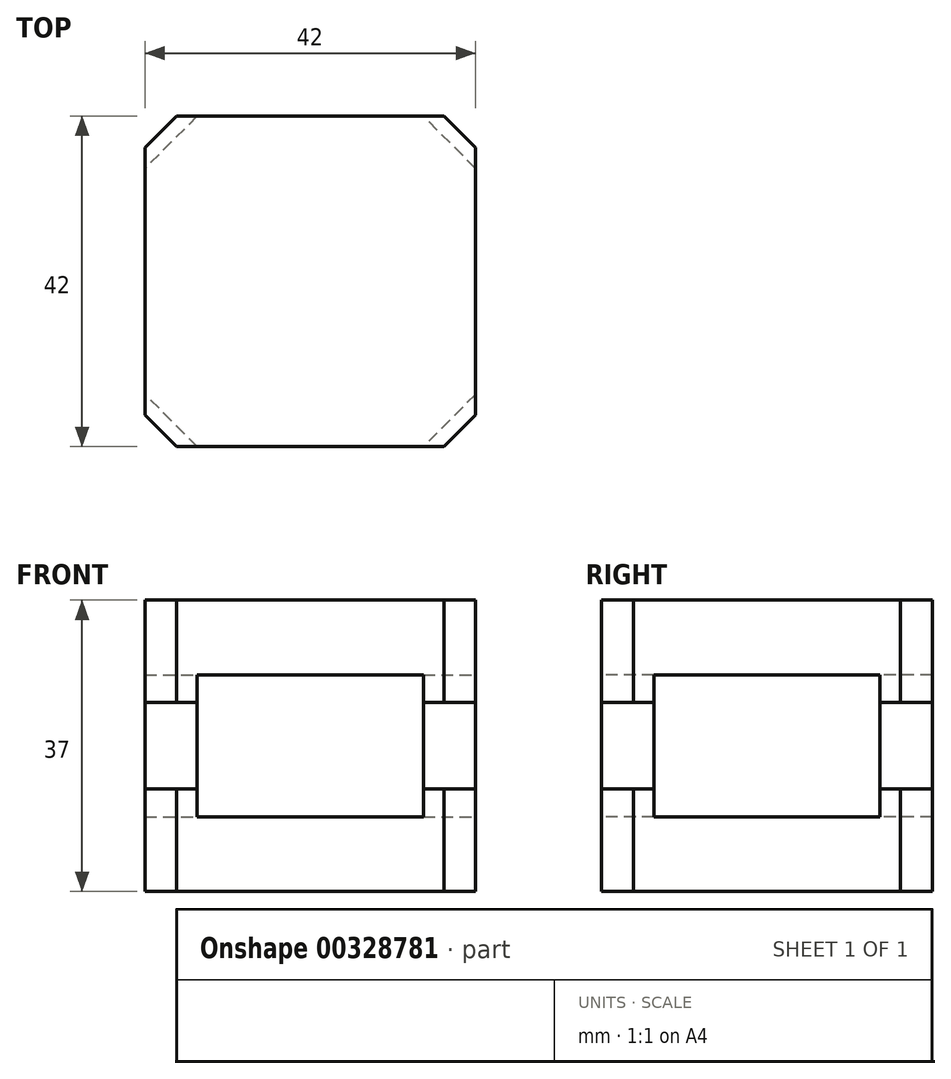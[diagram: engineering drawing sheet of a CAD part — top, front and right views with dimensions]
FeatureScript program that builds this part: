
annotation { "Feature Type Name" : "Feature", "Feature Type Description" : "" }
export const myFeature = defineFeature(function(context is Context, id is Id, definition is map)
    precondition{}
    {
        {
            var Q0;
            Q0=qCreatedBy(makeId("Top.planeOp"),FACE);
            var sketch = newSketch(context, id + "F0", { "sketchPlane" : qUnion([Q0])});
            skLineSegment(sketch, "E0.bottom", {"start": v(16.97, -21) * mm, "end": v(-16.97, -21) * mm});
            skLineSegment(sketch, "E0.top", {"start": v(16.97, 21) * mm, "end": v(-16.97, 21) * mm});
            skLineSegment(sketch, "E0.left", {"start": v(21, -16.97) * mm, "end": v(21, 16.97) * mm});
            skLineSegment(sketch, "E0.right", {"start": v(-21, -16.97) * mm, "end": v(-21, 16.97) * mm});
            skPoint(sketch, "E0.middle", {"position": v(0, 0) * mm});
            skLineSegment(sketch, "E1.bottom", {"start": v(-21, 16.97) * mm, "end": v(-16.97, 21) * mm});
            skLineSegment(sketch, "E1.top", {"start": v(16.97, -21) * mm, "end": v(21, -16.97) * mm});
            skLineSegment(sketch, "E1.left", {"start": v(-21, -16.97) * mm, "end": v(-16.97, -21) * mm});
            skLineSegment(sketch, "E1.right", {"start": v(16.97, 21) * mm, "end": v(21, 16.97) * mm});
            skLineSegment(sketch, "E2", {"start": v(21, 0) * mm, "end": v(0, 0) * mm, "construction": true});
            skLineSegment(sketch, "E3", {"start": v(0, 21) * mm, "end": v(0, 0) * mm, "construction": true});
            skSolve(sketch);
        }
        {
            var Q0;
            Q0=qSketchRegion(id+"F0",true);
            extrude(context, id + "F1", {"entities" : qUnion([Q0]), "depth" : 13 * mm});
        }
        {
            var Q0;
            Q0=qCreatedBy(makeId("Top.planeOp"),FACE);
            cPlane(context, id + "F2", {"entities" : qUnion([Q0]), "cplaneType" : CPlaneType.OFFSET, "offset" : 9.5 * mm, "width" : 150 * mm, "height" : 150 * mm});
        }
        {
            var Q0;
            Q0=qCreatedBy(id+"F2.planeOp",FACE);
            var sketch = newSketch(context, id + "F3", { "sketchPlane" : qUnion([Q0])});
            skLineSegment(sketch, "E4.bottom", {"start": v(14.36, -21) * mm, "end": v(-14.36, -21) * mm});
            skLineSegment(sketch, "E4.top", {"start": v(14.36, 21) * mm, "end": v(-14.36, 21) * mm});
            skLineSegment(sketch, "E4.left", {"start": v(21, -14.36) * mm, "end": v(21, 14.36) * mm});
            skLineSegment(sketch, "E4.right", {"start": v(-21, -14.36) * mm, "end": v(-21, 14.36) * mm});
            skPoint(sketch, "E4.middle", {"position": v(0, 0) * mm});
            skLineSegment(sketch, "E5.bottom", {"start": v(-21, 14.36) * mm, "end": v(-14.36, 21) * mm});
            skLineSegment(sketch, "E5.top", {"start": v(14.36, -21) * mm, "end": v(21, -14.36) * mm});
            skLineSegment(sketch, "E5.left", {"start": v(-21, -14.36) * mm, "end": v(-14.36, -21) * mm});
            skLineSegment(sketch, "E5.right", {"start": v(14.36, 21) * mm, "end": v(21, 14.36) * mm});
            skLineSegment(sketch, "E6", {"start": v(21, 0) * mm, "end": v(0, 0) * mm, "construction": true});
            skLineSegment(sketch, "E7", {"start": v(0, 21) * mm, "end": v(0, 0) * mm, "construction": true});
            skSolve(sketch);
        }
        {
            var Q0;
            Q0=qSketchRegion(id+"F3",true);
            extrude(context, id + "F4", {"entities" : qUnion([Q0]), "depth" : 18 * mm});
        }
        {
            var Q0;
            Q0=makeQuery(id+"F4.opExtrude","SWEPT_BODY",BODY,{"disambiguationData":[OSD([sQuery(id+"F3.wireOp",EDGE,"E4.bottom"),sQuery(id+"F3.wireOp",EDGE,"E4.top"),sQuery(id+"F3.wireOp",EDGE,"E4.left"),sQuery(id+"F3.wireOp",EDGE,"E4.right"),sQuery(id+"F3.wireOp",EDGE,"E5.bottom"),sQuery(id+"F3.wireOp",EDGE,"E5.top"),sQuery(id+"F3.wireOp",EDGE,"E5.left"),sQuery(id+"F3.wireOp",EDGE,"E5.right")])]});
            var Q1;
            Q1=makeQuery(id+"F1.opExtrude","SWEPT_BODY",BODY,{"disambiguationData":[OSD([sQuery(id+"F0.wireOp",EDGE,"E0.bottom"),sQuery(id+"F0.wireOp",EDGE,"E0.top"),sQuery(id+"F0.wireOp",EDGE,"E0.left"),sQuery(id+"F0.wireOp",EDGE,"E0.right"),sQuery(id+"F0.wireOp",EDGE,"E1.bottom"),sQuery(id+"F0.wireOp",EDGE,"E1.top"),sQuery(id+"F0.wireOp",EDGE,"E1.left"),sQuery(id+"F0.wireOp",EDGE,"E1.right")])]});
            booleanBodies(context, id + "F5", {"operationType" : BooleanOperationType.SUBTRACTION, "tools" : qUnion([Q0]), "targets" : qUnion([Q1]), "keepTools" : true});
        }
        {
            var Q0;
            Q0=makeQuery(id+"F4.opExtrude","CAP_FACE",FACE,{"disambiguationData":[OSD([sQuery(id+"F3.wireOp",EDGE,"E4.bottom"),sQuery(id+"F3.wireOp",EDGE,"E4.top"),sQuery(id+"F3.wireOp",EDGE,"E4.left"),sQuery(id+"F3.wireOp",EDGE,"E4.right"),sQuery(id+"F3.wireOp",EDGE,"E5.bottom"),sQuery(id+"F3.wireOp",EDGE,"E5.top"),sQuery(id+"F3.wireOp",EDGE,"E5.left"),sQuery(id+"F3.wireOp",EDGE,"E5.right")])],"isStart":false});
            cPlane(context, id + "F6", {"entities" : qUnion([Q0]), "cplaneType" : CPlaneType.OFFSET, "offset" : 3.5 * mm, "oppositeDirection" : true, "width" : 150 * mm, "height" : 150 * mm});
        }
        {
            var Q0;
            Q0=qCreatedBy(id+"F6.planeOp",FACE);
            var sketch = newSketch(context, id + "F7", { "sketchPlane" : qUnion([Q0])});
            skLineSegment(sketch, "E8.bottom", {"start": v(16.97, -21) * mm, "end": v(-16.97, -21) * mm});
            skLineSegment(sketch, "E8.top", {"start": v(16.97, 21) * mm, "end": v(-16.97, 21) * mm});
            skLineSegment(sketch, "E8.left", {"start": v(21, -16.97) * mm, "end": v(21, 16.97) * mm});
            skLineSegment(sketch, "E8.right", {"start": v(-21, -16.97) * mm, "end": v(-21, 16.97) * mm});
            skPoint(sketch, "E8.middle", {"position": v(0, 0) * mm});
            skLineSegment(sketch, "E9.bottom", {"start": v(-21, 16.97) * mm, "end": v(-16.97, 21) * mm});
            skLineSegment(sketch, "E9.top", {"start": v(16.97, -21) * mm, "end": v(21, -16.97) * mm});
            skLineSegment(sketch, "E9.left", {"start": v(-21, -16.97) * mm, "end": v(-16.97, -21) * mm});
            skLineSegment(sketch, "E9.right", {"start": v(16.97, 21) * mm, "end": v(21, 16.97) * mm});
            skLineSegment(sketch, "E10", {"start": v(21, 0) * mm, "end": v(0, 0) * mm, "construction": true});
            skLineSegment(sketch, "E11", {"start": v(0, 21) * mm, "end": v(0, 0) * mm, "construction": true});
            skSolve(sketch);
        }
        {
            var Q0;
            Q0=qSketchRegion(id+"F7",true);
            extrude(context, id + "F8", {"entities" : qUnion([Q0]), "depth" : 13 * mm});
        }
        {
            var Q0;
            Q0=makeQuery(id+"F4.opExtrude","SWEPT_BODY",BODY,{"disambiguationData":[OSD([sQuery(id+"F3.wireOp",EDGE,"E4.bottom"),sQuery(id+"F3.wireOp",EDGE,"E4.top"),sQuery(id+"F3.wireOp",EDGE,"E4.left"),sQuery(id+"F3.wireOp",EDGE,"E4.right"),sQuery(id+"F3.wireOp",EDGE,"E5.bottom"),sQuery(id+"F3.wireOp",EDGE,"E5.top"),sQuery(id+"F3.wireOp",EDGE,"E5.left"),sQuery(id+"F3.wireOp",EDGE,"E5.right")])]});
            var Q1;
            Q1=makeQuery(id+"F8.opExtrude","SWEPT_BODY",BODY,{"disambiguationData":[OSD([sQuery(id+"F7.wireOp",EDGE,"E8.bottom"),sQuery(id+"F7.wireOp",EDGE,"E8.top"),sQuery(id+"F7.wireOp",EDGE,"E8.left"),sQuery(id+"F7.wireOp",EDGE,"E8.right"),sQuery(id+"F7.wireOp",EDGE,"E9.bottom"),sQuery(id+"F7.wireOp",EDGE,"E9.top"),sQuery(id+"F7.wireOp",EDGE,"E9.left"),sQuery(id+"F7.wireOp",EDGE,"E9.right")])]});
            booleanBodies(context, id + "F9", {"operationType" : BooleanOperationType.SUBTRACTION, "tools" : qUnion([Q0]), "targets" : qUnion([Q1]), "keepTools" : true});
        }
    });
